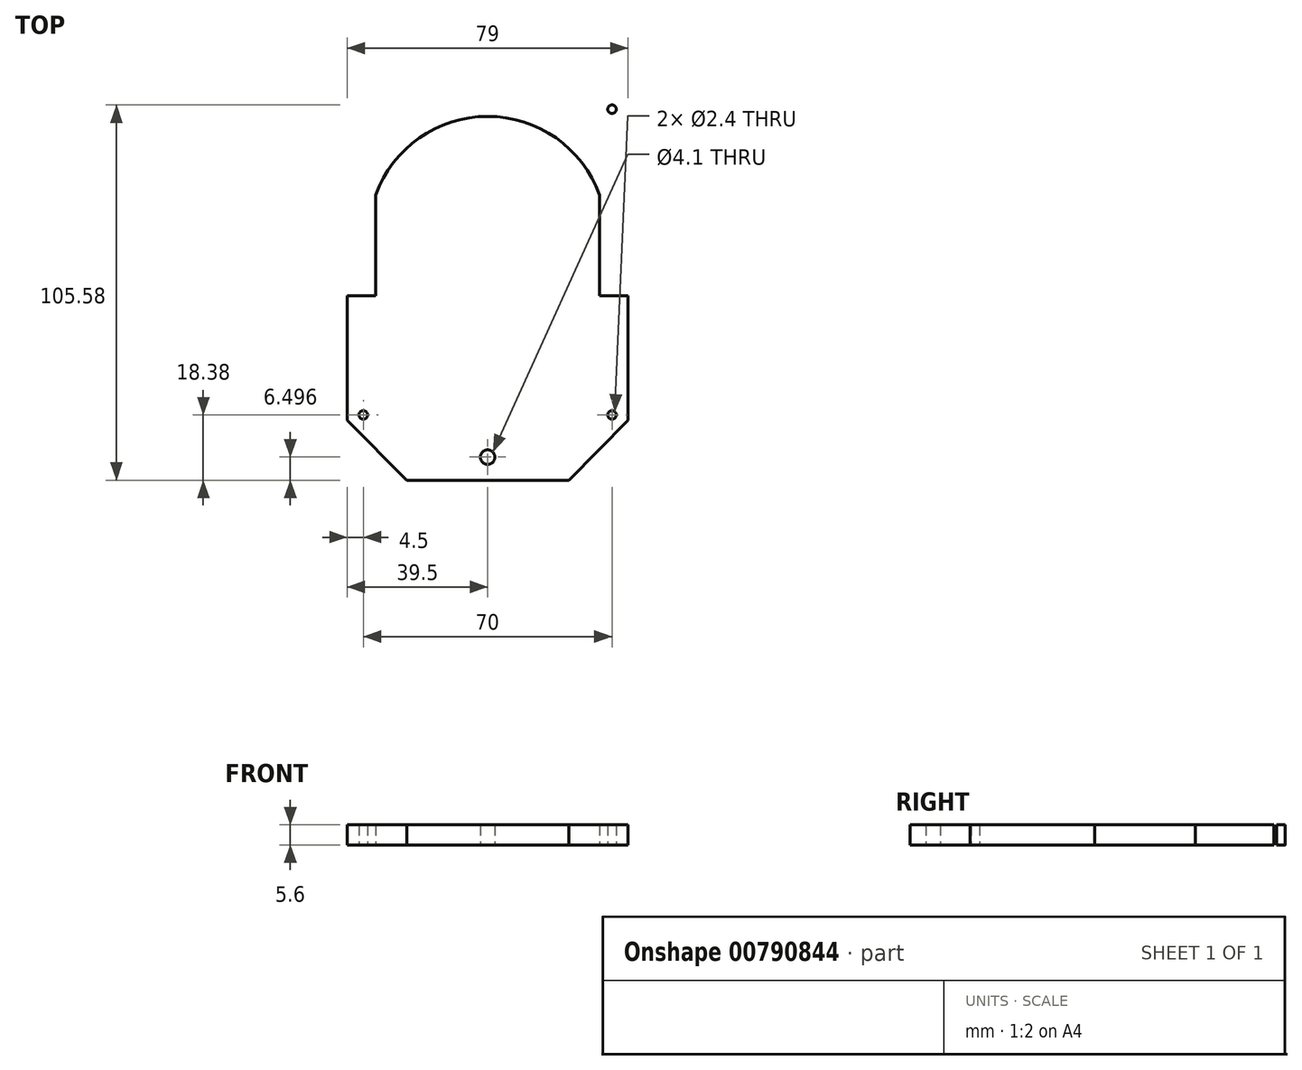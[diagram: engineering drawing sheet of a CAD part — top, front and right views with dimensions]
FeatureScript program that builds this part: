
annotation { "Feature Type Name" : "Feature", "Feature Type Description" : "" }
export const myFeature = defineFeature(function(context is Context, id is Id, definition is map)
    precondition{}
    {
        {
            var Q0;
            Q0=qCreatedBy(makeId("Top.planeOp"),FACE);
            var sketch = newSketch(context, id + "F0", { "sketchPlane" : qUnion([Q0])});
            skLineSegment(sketch, "E0.bottom", {"start": v(36.5, -47.5) * mm, "end": v(-36.5, -47.5) * mm, "construction": true});
            skLineSegment(sketch, "E0.top", {"start": v(36.5, 47.5) * mm, "end": v(-36.5, 47.5) * mm, "construction": true});
            skLineSegment(sketch, "E0.left", {"start": v(39.5, -44.5) * mm, "end": v(39.5, 44.5) * mm});
            skLineSegment(sketch, "E0.right", {"start": v(-39.5, -44.5) * mm, "end": v(-39.5, 44.5) * mm});
            skPoint(sketch, "E0.middle", {"position": v(0, 0) * mm});
            skCircle(sketch, "E1", {"center": v(35, -43) * mm, "radius": 1.2 * mm});
            skLineSegment(sketch, "E2", {"start": v(0, 0) * mm, "end": v(59.48, 0) * mm, "construction": true});
            skLineSegment(sketch, "E3", {"start": v(0, -16.17) * mm, "end": v(0, 69.78) * mm, "construction": true});
            skCircle(sketch, "E4.MirrorC", {"center": v(35, 43) * mm, "radius": 1.2 * mm});
            skCircle(sketch, "E5.MirrorC", {"center": v(-35, 43) * mm, "radius": 1.2 * mm});
            skCircle(sketch, "E6.MirrorC", {"center": v(-35, -43) * mm, "radius": 1.2 * mm});
            skPoint(sketch, "E7.visualSharp", {"position": v(-39.5, 47.5) * mm});
            skArc(sketch, "E7.filletArc", {"start": v(-36.5, 47.5) * mm, "mid": v(-38.62, 46.62) * mm, "end": v(-39.5, 44.5) * mm, "construction": true});
            skPoint(sketch, "E8.visualSharp", {"position": v(39.5, 47.5) * mm});
            skArc(sketch, "E8.filletArc", {"start": v(39.5, 44.5) * mm, "mid": v(38.62, 46.62) * mm, "end": v(36.5, 47.5) * mm, "construction": true});
            skPoint(sketch, "E9.visualSharp", {"position": v(39.5, -47.5) * mm});
            skArc(sketch, "E9.filletArc", {"start": v(36.5, -47.5) * mm, "mid": v(38.62, -46.62) * mm, "end": v(39.5, -44.5) * mm, "construction": true});
            skPoint(sketch, "E10.visualSharp", {"position": v(-39.5, -47.5) * mm});
            skArc(sketch, "E10.filletArc", {"start": v(-39.5, -44.5) * mm, "mid": v(-38.62, -46.62) * mm, "end": v(-36.5, -47.5) * mm, "construction": true});
            skCircle(sketch, "E11", {"center": v(0, 7.5) * mm, "radius": 33.5 * mm});
            skLineSegment(sketch, "E12.bottom", {"start": v(31, -23.5) * mm, "end": v(-31, -23.5) * mm, "construction": true});
            skLineSegment(sketch, "E12.top", {"start": v(31, 38.5) * mm, "end": v(-31, 38.5) * mm, "construction": true});
            skLineSegment(sketch, "E12.left", {"start": v(31, -23.5) * mm, "end": v(31, 38.5) * mm, "construction": true});
            skLineSegment(sketch, "E12.right", {"start": v(-31, -23.5) * mm, "end": v(-31, 38.5) * mm, "construction": true});
            skLineSegment(sketch, "E13", {"start": v(0, 61.38) * mm, "end": v(22.8, 61.38) * mm});
            skLineSegment(sketch, "E14", {"start": v(22.8, 61.38) * mm, "end": v(39.5, 44.5) * mm});
            skLineSegment(sketch, "E15.MirrorCS", {"start": v(-22.8, 61.38) * mm, "end": v(-39.5, 44.5) * mm});
            skLineSegment(sketch, "E16.MirrorCS", {"start": v(0, 61.38) * mm, "end": v(-22.8, 61.38) * mm});
            skCircle(sketch, "E17", {"center": v(0, 54.88) * mm, "radius": 2.05 * mm});
            skLineSegment(sketch, "E18.MirrorCS", {"start": v(-22.8, -61.38) * mm, "end": v(-39.5, -44.5) * mm});
            skLineSegment(sketch, "E19.MirrorCS", {"start": v(0, -61.38) * mm, "end": v(-22.8, -61.38) * mm});
            skLineSegment(sketch, "E20.MirrorCS", {"start": v(0, -61.38) * mm, "end": v(22.8, -61.38) * mm});
            skLineSegment(sketch, "E21.MirrorCS", {"start": v(22.8, -61.38) * mm, "end": v(39.5, -44.5) * mm});
            skArc(sketch, "E22.MirrorCS", {"start": v(-39.5, 44.5) * mm, "mid": v(-38.62, 46.62) * mm, "end": v(-36.5, 47.5) * mm, "construction": true});
            skArc(sketch, "E23.MirrorCS", {"start": v(36.5, 47.5) * mm, "mid": v(38.62, 46.62) * mm, "end": v(39.5, 44.5) * mm, "construction": true});
            skCircle(sketch, "E24.MirrorC", {"center": v(0, -54.88) * mm, "radius": 2.05 * mm});
            skLineSegment(sketch, "E25", {"start": v(-51.45, 25.5) * mm, "end": v(82.98, 25.5) * mm, "construction": true});
            skLineSegment(sketch, "E26", {"start": v(-59.5, -9.5) * mm, "end": v(81.33, -9.5) * mm, "construction": true});
            skLineSegment(sketch, "E27", {"start": v(31.5, 25.5) * mm, "end": v(31.5, -9.5) * mm});
            skLineSegment(sketch, "E28.MirrorCS", {"start": v(-31.5, 25.5) * mm, "end": v(-31.5, -9.5) * mm});
            skLineSegment(sketch, "E29", {"start": v(31.5, 25.5) * mm, "end": v(39.5, 25.5) * mm});
            skLineSegment(sketch, "E30", {"start": v(31.5, -9.5) * mm, "end": v(39.5, -9.5) * mm});
            skLineSegment(sketch, "E31", {"start": v(-31.5, -9.5) * mm, "end": v(-39.5, -9.5) * mm});
            skLineSegment(sketch, "E32", {"start": v(-31.5, 25.5) * mm, "end": v(-39.5, 25.5) * mm});
            skSolve(sketch);
        }
        {
            var Q0;
            Q0=makeQuery(id+"F0.imprint","IMPRINT",FACE,{"disambiguationData":[TD([[makeQuery(id+"F0.imprint","IMPRINT",EDGE,{"derivedFrom":sQuery(id+"F0.wireOp",EDGE,"E4.MirrorC")}),1.0]])]});
            var Q1;
            {var subQ0=sQuery(id+"F0.wireOp",EDGE,"E28.MirrorCS");var subQ1=sQuery(id+"F0.wireOp",EDGE,"E11");var subQ2=makeQuery(id+"F0.imprint","INTERSECT",VERTEX,{"disambiguationData":[OD(0.0)],"derivedFrom":[subQ1,subQ0]});Q1=makeQuery(id+"F0.imprint","IMPRINT",FACE,{"disambiguationData":[TD([[makeQuery(id+"F0.imprint","IMPRINT",EDGE,{"disambiguationData":[TD([[subQ2,1.0]])],"derivedFrom":subQ1}),1.0]])]});}
            var Q2;
            Q2=makeQuery(id+"F0.imprint","IMPRINT",FACE,{"disambiguationData":[TD([[makeQuery(id+"F0.imprint","IMPRINT",EDGE,{"derivedFrom":sQuery(id+"F0.wireOp",EDGE,"E1")}),-1.0]])]});
            extrude(context, id + "F1", {"entities" : qUnion([Q0, Q1, Q2]), "depth" : 5.6 * mm, "offsetDistance" : 25 * mm});
        }
    });
